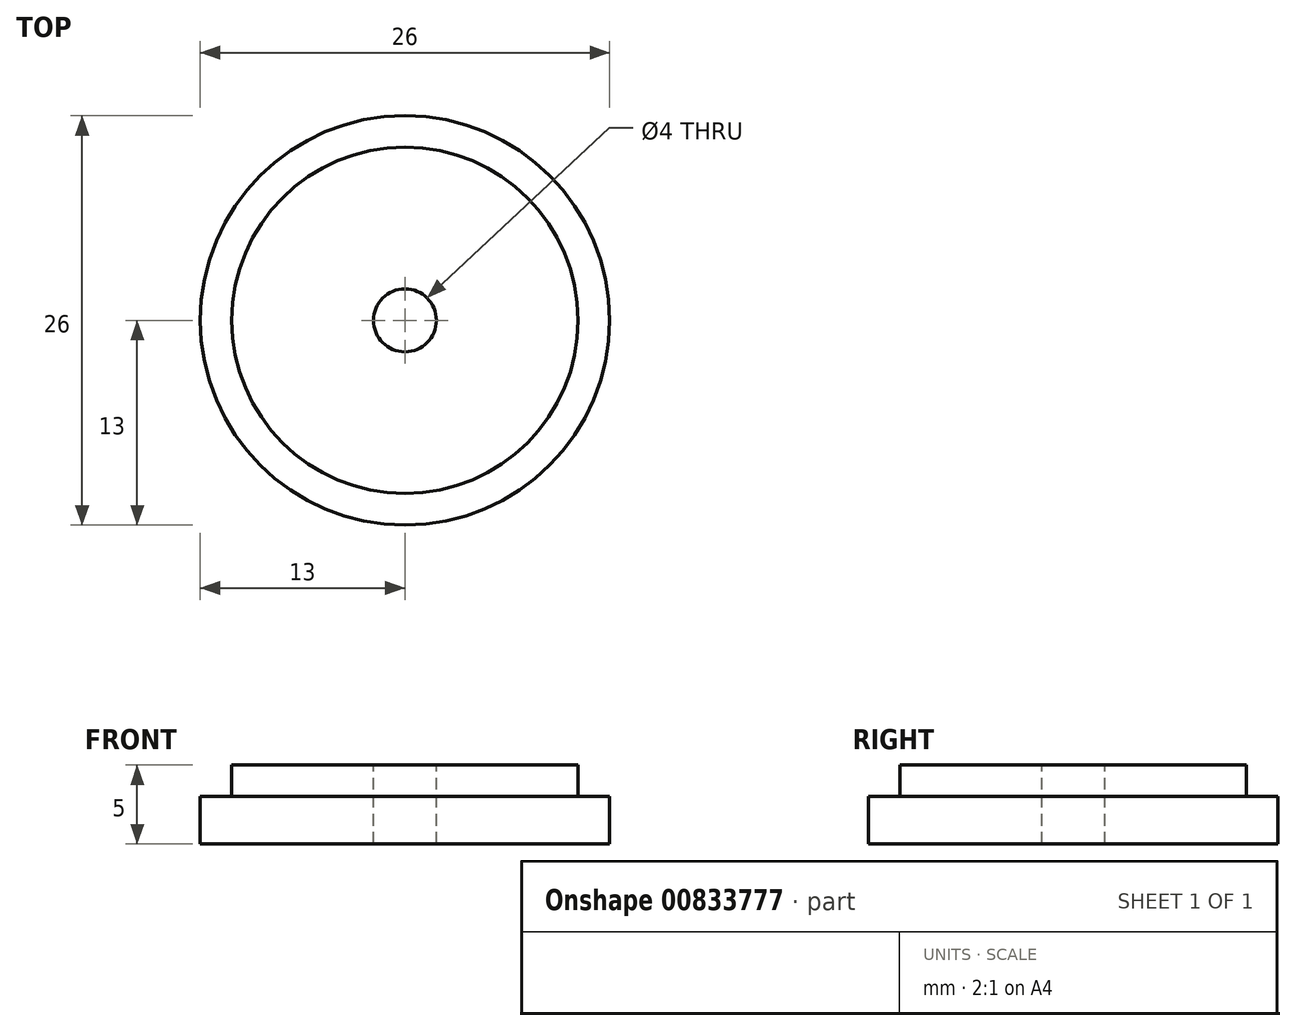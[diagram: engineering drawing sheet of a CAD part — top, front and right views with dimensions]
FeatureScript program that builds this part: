
annotation { "Feature Type Name" : "Feature", "Feature Type Description" : "" }
export const myFeature = defineFeature(function(context is Context, id is Id, definition is map)
    precondition{}
    {
        {
            var Q0;
            Q0=qCreatedBy(makeId("Front.planeOp"),FACE);
            var sketch = newSketch(context, id + "F0", { "sketchPlane" : qUnion([Q0])});
            skLineSegment(sketch, "E0.bottom", {"start": v(2, 0) * mm, "end": v(13, 0) * mm});
            skLineSegment(sketch, "E0.top", {"start": v(11, 3) * mm, "end": v(13, 3) * mm});
            skLineSegment(sketch, "E0.right", {"start": v(13, 0) * mm, "end": v(13, 3) * mm});
            skLineSegment(sketch, "E1.top", {"start": v(2, 5) * mm, "end": v(11, 5) * mm});
            skLineSegment(sketch, "E1.right", {"start": v(11, 3) * mm, "end": v(11, 5) * mm});
            skLineSegment(sketch, "E2", {"start": v(2, 0) * mm, "end": v(2, 5) * mm});
            skLineSegment(sketch, "E3", {"start": v(0, 14.6) * mm, "end": v(0, -8.15) * mm, "construction": true});
            skSolve(sketch);
        }
        {
            var Q0;
            Q0 = qSketchRegion(id + "F0", true);
            var Q1;
            Q1=sQuery(id+"F0.wireOp",EDGE,"E3");
            revolve(context, id + "F1", {"surfaceOperationType" : NewSurfaceOperationType.NEW, "entities" : qUnion([Q0]), "axis" : qUnion([Q1]), "revolveType" : RevolveType.FULL});
        }
    });
